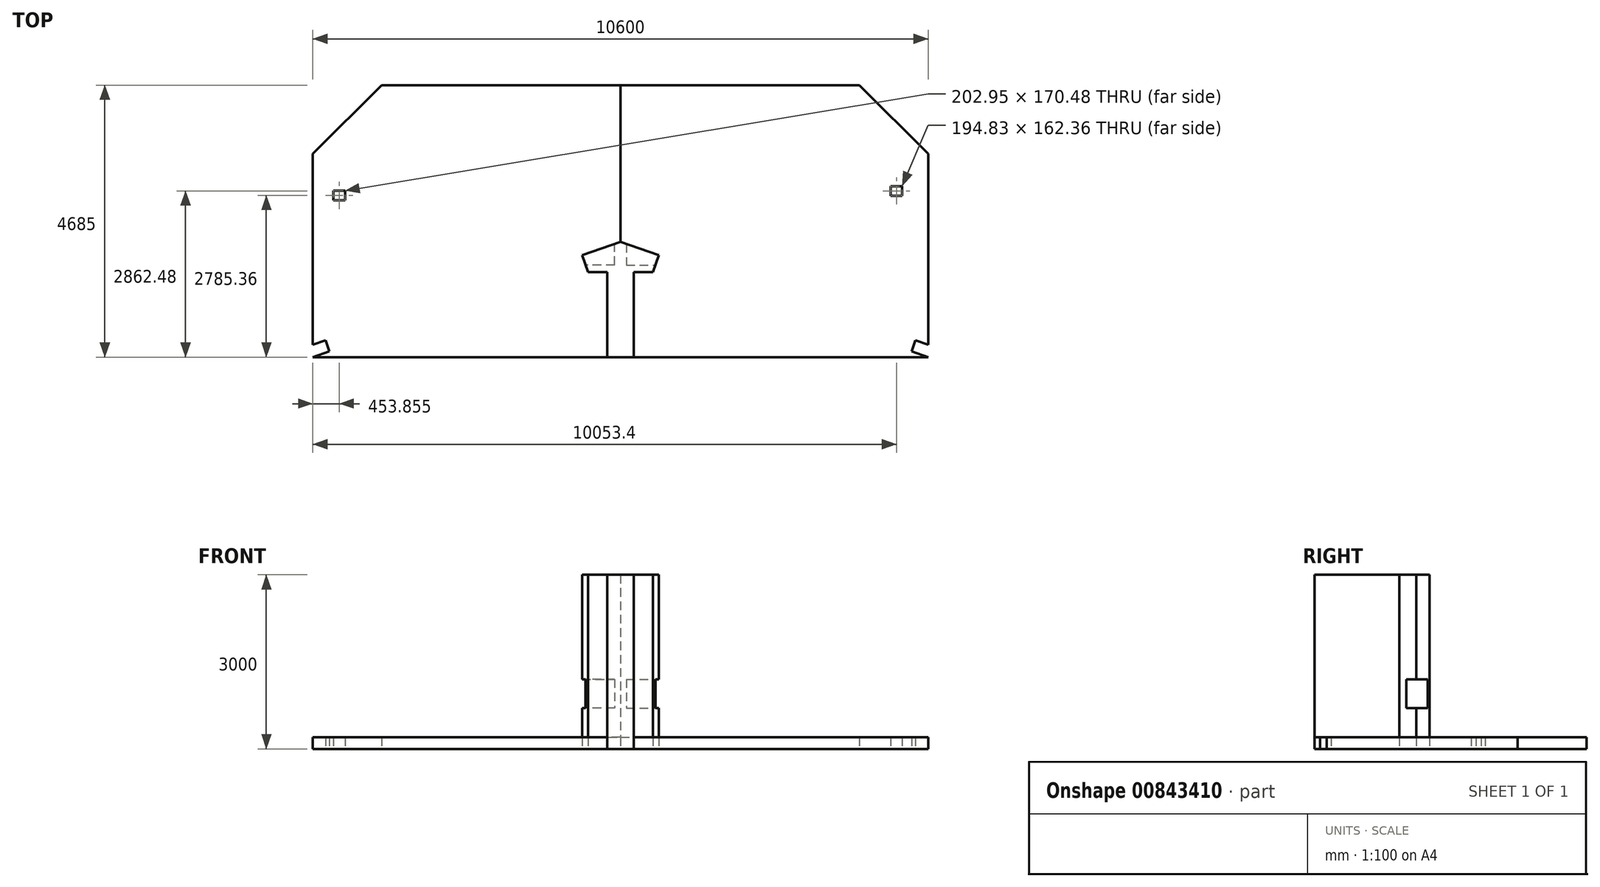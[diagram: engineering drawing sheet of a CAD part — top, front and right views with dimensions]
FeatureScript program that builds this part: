
annotation { "Feature Type Name" : "Feature", "Feature Type Description" : "" }
export const myFeature = defineFeature(function(context is Context, id is Id, definition is map)
    precondition{}
    {
        {
            var Q0;
            Q0=qCreatedBy(makeId("Top.planeOp"),FACE);
            var sketch = newSketch(context, id + "F0", { "sketchPlane" : qUnion([Q0])});
            skLineSegment(sketch, "E0.bottom", {"start": v(-2879.78, 2584.02) * mm, "end": v(-1580.4, 2584.02) * mm});
            skLineSegment(sketch, "E0.top", {"start": v(-2879.78, 1773.08) * mm, "end": v(-1580.4, 1773.08) * mm});
            skLineSegment(sketch, "E0.left", {"start": v(-2879.78, 2584.02) * mm, "end": v(-2879.78, 1773.08) * mm});
            skLineSegment(sketch, "E0.right", {"start": v(-1580.4, 2584.02) * mm, "end": v(-1580.4, 1773.08) * mm});
            skLineSegment(sketch, "E1.bottom", {"start": v(291.18, 2556.08) * mm, "end": v(2223.4, 2556.08) * mm});
            skLineSegment(sketch, "E1.top", {"start": v(291.18, 1660.2) * mm, "end": v(2223.4, 1660.2) * mm});
            skLineSegment(sketch, "E1.left", {"start": v(291.18, 2556.08) * mm, "end": v(291.18, 1660.2) * mm});
            skLineSegment(sketch, "E1.right", {"start": v(2223.4, 2556.08) * mm, "end": v(2223.4, 1660.2) * mm});
            skLineSegment(sketch, "E2.bottom", {"start": v(3957.7, 594.24) * mm, "end": v(4737.35, 594.24) * mm});
            skLineSegment(sketch, "E2.top", {"start": v(3957.7, -525.95) * mm, "end": v(4737.35, -525.95) * mm});
            skLineSegment(sketch, "E2.left", {"start": v(3957.7, 594.24) * mm, "end": v(3957.7, -525.95) * mm});
            skLineSegment(sketch, "E2.right", {"start": v(4737.35, 594.24) * mm, "end": v(4737.35, -525.95) * mm});
            skLineSegment(sketch, "E3.bottom", {"start": v(-4506.24, -591.91) * mm, "end": v(-3473.46, -591.91) * mm});
            skLineSegment(sketch, "E3.top", {"start": v(-4506.24, -1546.94) * mm, "end": v(-3473.46, -1546.94) * mm});
            skLineSegment(sketch, "E3.left", {"start": v(-4506.24, -591.91) * mm, "end": v(-4506.24, -1546.94) * mm});
            skLineSegment(sketch, "E3.right", {"start": v(-3473.46, -591.91) * mm, "end": v(-3473.46, -1546.94) * mm});
            skSolve(sketch);
        }
        {
            var Q0;
            Q0=qCreatedBy(makeId("Top.planeOp"),FACE);
            var sketch = newSketch(context, id + "F1", { "sketchPlane" : qUnion([Q0])});
            skLineSegment(sketch, "E4.bottom", {"start": v(-4115, 2342.5) * mm, "end": v(4115, 2342.5) * mm});
            skLineSegment(sketch, "E4.top", {"start": v(-5300, -2342.5) * mm, "end": v(-230.94, -2342.5) * mm});
            skLineSegment(sketch, "E4.left", {"start": v(-5300, 1157.5) * mm, "end": v(-5300, -2342.5) * mm});
            skLineSegment(sketch, "E4.right", {"start": v(5300, 1157.5) * mm, "end": v(5300, -2342.5) * mm});
            skPoint(sketch, "E4.middle", {"position": v(0, 0) * mm});
            skLineSegment(sketch, "E5", {"start": v(-5300, 1157.5) * mm, "end": v(-4115, 2342.5) * mm});
            skLineSegment(sketch, "E6", {"start": v(4115, 2342.5) * mm, "end": v(5300, 1157.5) * mm});
            skPoint(sketch, "E7.orphan", {"position": v(5300, 2342.5) * mm});
            skPoint(sketch, "E8.orphan", {"position": v(-5300, 2342.5) * mm});
            skLineSegment(sketch, "E9", {"start": v(0, -357.5) * mm, "end": v(661.86, -585.4) * mm});
            skLineSegment(sketch, "E10", {"start": v(0, -357.5) * mm, "end": v(-661.86, -585.4) * mm});
            skLineSegment(sketch, "E11", {"start": v(-661.86, -585.4) * mm, "end": v(-560.94, -878.5) * mm});
            skLineSegment(sketch, "E12", {"start": v(-230.94, -878.5) * mm, "end": v(-230.94, -2342.5) * mm});
            skLineSegment(sketch, "E13", {"start": v(0, 0) * mm, "end": v(0, 2342.5) * mm, "construction": true});
            skLineSegment(sketch, "E14.MirrorCS", {"start": v(230.94, -878.5) * mm, "end": v(230.94, -2342.5) * mm});
            skLineSegment(sketch, "E15.MirrorCS", {"start": v(661.86, -585.4) * mm, "end": v(560.94, -878.5) * mm});
            skLineSegment(sketch, "E16.MirrorCS", {"start": v(560.94, -878.5) * mm, "end": v(230.94, -878.5) * mm});
            skLineSegment(sketch, "E17.trimOffspring", {"start": v(230.94, -2342.5) * mm, "end": v(5300, -2342.5) * mm});
            skLineSegment(sketch, "E18", {"start": v(-230.94, -878.5) * mm, "end": v(-560.94, -878.5) * mm});
            skLineSegment(sketch, "E19.bottom", {"start": v(4850.85, 601.16) * mm, "end": v(4656.02, 601.16) * mm});
            skLineSegment(sketch, "E19.top", {"start": v(4850.85, 438.8) * mm, "end": v(4656.02, 438.8) * mm});
            skLineSegment(sketch, "E19.left", {"start": v(4850.85, 601.16) * mm, "end": v(4850.85, 438.8) * mm});
            skLineSegment(sketch, "E19.right", {"start": v(4656.02, 601.16) * mm, "end": v(4656.02, 438.8) * mm});
            skLineSegment(sketch, "E20.bottom", {"start": v(-4947.62, 528.1) * mm, "end": v(-4744.67, 528.1) * mm});
            skLineSegment(sketch, "E20.top", {"start": v(-4947.62, 357.62) * mm, "end": v(-4744.67, 357.62) * mm});
            skLineSegment(sketch, "E20.left", {"start": v(-4947.62, 528.1) * mm, "end": v(-4947.62, 357.62) * mm});
            skLineSegment(sketch, "E20.right", {"start": v(-4744.67, 528.1) * mm, "end": v(-4744.67, 357.62) * mm});
            skLineSegment(sketch, "E21", {"start": v(-230.94, -2342.5) * mm, "end": v(230.94, -2342.5) * mm});
            skLineSegment(sketch, "E22", {"start": v(-5300, -2130.98) * mm, "end": v(-5081.46, -2055.73) * mm});
            skLineSegment(sketch, "E23", {"start": v(-5081.46, -2055.73) * mm, "end": v(-5016.34, -2244.83) * mm});
            skLineSegment(sketch, "E24", {"start": v(-5016.34, -2244.83) * mm, "end": v(-5300, -2342.5) * mm});
            skLineSegment(sketch, "E25.MirrorCS", {"start": v(5016.34, -2244.83) * mm, "end": v(5300, -2342.5) * mm});
            skLineSegment(sketch, "E26.MirrorCS", {"start": v(5300, -2130.98) * mm, "end": v(5081.46, -2055.73) * mm});
            skLineSegment(sketch, "E27.MirrorCS", {"start": v(5081.46, -2055.73) * mm, "end": v(5016.34, -2244.83) * mm});
            skLineSegment(sketch, "E28", {"start": v(0, -357.5) * mm, "end": v(0, 2342.5) * mm});
            skSolve(sketch);
        }
        {
            var Q0;
            Q0=makeQuery(id+"F1.imprint","IMPRINT",FACE,{"disambiguationData":[TD([[makeQuery(id+"F1.imprint","IMPRINT",EDGE,{"derivedFrom":sQuery(id+"F1.wireOp",EDGE,"E4.top")}),1.0]])]});
            extrude(context, id + "F2", {"entities" : qUnion([Q0]), "depth" : 200 * mm, "offsetDistance" : 25 * mm});
        }
        {
            var Q0;
            {var subQ0=sQuery(id+"F1.wireOp",EDGE,"E6");Q0=makeQuery(id+"F1.imprint","IMPRINT",FACE,{"disambiguationData":[TD([[makeQuery(id+"F1.imprint","IMPRINT",EDGE,{"derivedFrom":subQ0}),-1.0]])]});}
            extrude(context, id + "F3", {"entities" : qUnion([Q0]), "depth" : 200 * mm, "offsetDistance" : 25 * mm});
        }
        {
            var Q0;
            Q0=makeQuery(id+"F1.imprint","IMPRINT",FACE,{"disambiguationData":[TD([[makeQuery(id+"F1.imprint","IMPRINT",EDGE,{"derivedFrom":sQuery(id+"F1.wireOp",EDGE,"E11")}),1.0]])]});
            extrude(context, id + "F4", {"entities" : qUnion([Q0]), "depth" : 3000 * mm, "offsetDistance" : 25 * mm});
        }
        {
            var Q0;
            Q0=makeQuery(id+"F2.opExtrude","CAP_FACE",FACE,{"disambiguationData":[OSD([sQuery(id+"F1.wireOp",EDGE,"E4.bottom"),sQuery(id+"F1.wireOp",EDGE,"E4.top"),sQuery(id+"F1.wireOp",EDGE,"E4.left"),sQuery(id+"F1.wireOp",EDGE,"E5"),sQuery(id+"F1.wireOp",EDGE,"E11"),sQuery(id+"F1.wireOp",EDGE,"E12"),sQuery(id+"F1.wireOp",EDGE,"E10"),sQuery(id+"F1.wireOp",EDGE,"E18"),sQuery(id+"F1.wireOp",EDGE,"E20.bottom"),sQuery(id+"F1.wireOp",EDGE,"E20.top"),sQuery(id+"F1.wireOp",EDGE,"E20.left"),sQuery(id+"F1.wireOp",EDGE,"E20.right"),sQuery(id+"F1.wireOp",EDGE,"E22"),sQuery(id+"F1.wireOp",EDGE,"E23"),sQuery(id+"F1.wireOp",EDGE,"E24"),sQuery(id+"F1.wireOp",EDGE,"E28")])],"isStart":false});
            var sketch = newSketch(context, id + "F5", { "sketchPlane" : qUnion([Q0])});
            skLineSegment(sketch, "E29.bottom", {"start": v(-700, 2342.5) * mm, "end": v(700, 2342.5) * mm});
            skLineSegment(sketch, "E29.top", {"start": v(-700, 1642.5) * mm, "end": v(700, 1642.5) * mm});
            skLineSegment(sketch, "E29.left", {"start": v(-700, 2342.5) * mm, "end": v(-700, 1642.5) * mm});
            skLineSegment(sketch, "E29.right", {"start": v(700, 2342.5) * mm, "end": v(700, 1642.5) * mm});
            skLineSegment(sketch, "E30", {"start": v(-661.86, -585.4) * mm, "end": v(661.86, -585.4) * mm});
            skLineSegment(sketch, "E31", {"start": v(-700, 1642.5) * mm, "end": v(-700, -757.5) * mm});
            skLineSegment(sketch, "E32", {"start": v(700, 1642.5) * mm, "end": v(700, -757.5) * mm});
            skLineSegment(sketch, "E33", {"start": v(0, -757.5) * mm, "end": v(0, 1642.5) * mm});
            skLineSegment(sketch, "E34", {"start": v(-700, -757.5) * mm, "end": v(700, -757.5) * mm});
            skLineSegment(sketch, "E35", {"start": v(-661.86, -757.5) * mm, "end": v(-661.86, -585.4) * mm});
            skLineSegment(sketch, "E36", {"start": v(-661.86, -757.5) * mm, "end": v(0, -757.5) * mm});
            skLineSegment(sketch, "E37.MirrorCS", {"start": v(661.86, -757.5) * mm, "end": v(0, -757.5) * mm});
            skLineSegment(sketch, "E38.MirrorCS", {"start": v(661.86, -757.5) * mm, "end": v(661.86, -585.4) * mm});
            skLineSegment(sketch, "E39", {"start": v(661.86, -585.4) * mm, "end": v(0, -357.5) * mm});
            skLineSegment(sketch, "E40", {"start": v(0, -357.5) * mm, "end": v(-661.86, -585.4) * mm});
            skSolve(sketch);
        }
        {
            var Q0;
            {var subQ3=sQuery(id+"F5.wireOp",EDGE,"E29.left");Q0=makeQuery(id+"F5.imprint","IMPRINT",FACE,{"disambiguationData":[TD([[makeQuery(id+"F5.imprint","IMPRINT",EDGE,{"derivedFrom":subQ3}),1.0]])]});}
            var Q1;
            {var subQ3=sQuery(id+"F5.wireOp",EDGE,"E29.right");Q1=makeQuery(id+"F5.imprint","IMPRINT",FACE,{"disambiguationData":[TD([[makeQuery(id+"F5.imprint","IMPRINT",EDGE,{"derivedFrom":subQ3}),-1.0]])]});}
            extrude(context, id + "F6", {"entities" : qUnion([Q0, Q1]), "depth" : 500 * mm, "offsetDistance" : 25 * mm});
        }
        {
            var Q0;
            {var subQ1=sQuery(id+"F5.wireOp",EDGE,"E32");Q0=makeQuery(id+"F5.imprint","IMPRINT",FACE,{"disambiguationData":[TD([[makeQuery(id+"F5.imprint","IMPRINT",EDGE,{"derivedFrom":subQ1}),-1.0]])]});}
            extrude(context, id + "F7", {"entities" : qUnion([Q0]), "depth" : 1000 * mm, "offsetDistance" : 25 * mm});
        }
        {
            var Q0;
            {var subQ1=sQuery(id+"F5.wireOp",EDGE,"E31");Q0=makeQuery(id+"F5.imprint","IMPRINT",FACE,{"disambiguationData":[TD([[makeQuery(id+"F5.imprint","IMPRINT",EDGE,{"derivedFrom":subQ1}),1.0]])]});}
            extrude(context, id + "F8", {"entities" : qUnion([Q0]), "depth" : 1000 * mm, "offsetDistance" : 25 * mm});
        }
        {
            var Q0;
            {var subQ0=sQuery(id+"F5.wireOp",EDGE,"E37.MirrorCS");Q0=makeQuery(id+"F5.imprint","IMPRINT",FACE,{"disambiguationData":[TD([[makeQuery(id+"F5.imprint","IMPRINT",EDGE,{"derivedFrom":subQ0}),1.0]])]});}
            var Q1;
            Q1=makeQuery(id+"F5.imprint","IMPRINT",FACE,{"disambiguationData":[TD([[makeQuery(id+"F5.imprint","IMPRINT",EDGE,{"derivedFrom":sQuery(id+"F5.wireOp",EDGE,"E35")}),-1.0]])]});
            extrude(context, id + "F9", {"entities" : qUnion([Q0, Q1]), "depth" : 1000 * mm, "offsetDistance" : 25 * mm});
        }
        {
            var Q0;
            Q0=makeQuery(id+"F7.opExtrude","SWEPT_FACE",FACE,{"disambiguationData":[OSD([sQuery(id+"F5.wireOp",EDGE,"E32")])]});
            var sketch = newSketch(context, id + "F10", { "sketchPlane" : qUnion([Q0])});
            skLineSegment(sketch, "E41.bottom", {"start": v(1642.5, 1200) * mm, "end": v(-757.5, 1200) * mm});
            skLineSegment(sketch, "E41.top", {"start": v(1642.5, 700) * mm, "end": v(-757.5, 700) * mm});
            skLineSegment(sketch, "E41.left", {"start": v(1642.5, 1200) * mm, "end": v(1642.5, 700) * mm});
            skLineSegment(sketch, "E41.right", {"start": v(-757.5, 1200) * mm, "end": v(-757.5, 700) * mm});
            skSolve(sketch);
        }
        {
            var Q0;
            Q0 = qSketchRegion(id + "F10", true);
            extrude(context, id + "F11", {"entities" : qUnion([Q0]), "operationType" : NewBodyOperationType.REMOVE, "oppositeDirection" : true, "depth" : 600 * mm, "offsetDistance" : 25 * mm});
        }
        {
            var Q0;
            Q0=makeQuery(id+"F8.opExtrude","SWEPT_FACE",FACE,{"disambiguationData":[OSD([sQuery(id+"F5.wireOp",EDGE,"E31")])]});
            var sketch = newSketch(context, id + "F12", { "sketchPlane" : qUnion([Q0])});
            skLineSegment(sketch, "E42.bottom", {"start": v(757.5, 1200) * mm, "end": v(-1642.5, 1200) * mm});
            skLineSegment(sketch, "E42.top", {"start": v(757.5, 700) * mm, "end": v(-1642.5, 700) * mm});
            skLineSegment(sketch, "E42.left", {"start": v(757.5, 1200) * mm, "end": v(757.5, 700) * mm});
            skLineSegment(sketch, "E42.right", {"start": v(-1642.5, 1200) * mm, "end": v(-1642.5, 700) * mm});
            skSolve(sketch);
        }
        {
            var Q0;
            Q0 = qSketchRegion(id + "F12", true);
            extrude(context, id + "F13", {"entities" : qUnion([Q0]), "operationType" : NewBodyOperationType.REMOVE, "oppositeDirection" : true, "depth" : 600 * mm, "offsetDistance" : 25 * mm});
        }
        {
            var Q0;
            Q0=makeQuery(id+"F6.opExtrude","CAP_FACE",FACE,{"disambiguationData":[OSD([sQuery(id+"F5.wireOp",EDGE,"E29.bottom"),sQuery(id+"F5.wireOp",EDGE,"E29.top"),sQuery(id+"F5.wireOp",EDGE,"E29.left"),sQuery(id+"F5.wireOp",EDGE,"E29.right")])],"isStart":false});
            var sketch = newSketch(context, id + "F14", { "sketchPlane" : qUnion([Q0])});
            skLineSegment(sketch, "E43.bottom", {"start": v(100, 1642.5) * mm, "end": v(-100, 1642.5) * mm});
            skLineSegment(sketch, "E43.top", {"start": v(100, 2342.5) * mm, "end": v(-100, 2342.5) * mm});
            skLineSegment(sketch, "E43.left", {"start": v(100, 1642.5) * mm, "end": v(100, 2342.5) * mm});
            skLineSegment(sketch, "E43.right", {"start": v(-100, 1642.5) * mm, "end": v(-100, 2342.5) * mm});
            skSolve(sketch);
        }
        {
            var Q0;
            Q0 = qSketchRegion(id + "F14", true);
            var Q1;
            Q1=makeQuery(id+"F8.opExtrude","CAP_FACE",FACE,{"disambiguationData":[OSD([sQuery(id+"F5.wireOp",EDGE,"E29.top"),sQuery(id+"F5.wireOp",EDGE,"E31"),sQuery(id+"F5.wireOp",EDGE,"E33"),sQuery(id+"F5.wireOp",EDGE,"E34"),sQuery(id+"F5.wireOp",EDGE,"E36")])],"isStart":false});
            extrude(context, id + "F15", {"entities" : qUnion([Q0]), "endBound" : BoundingType.UP_TO_SURFACE, "depth" : 25 * mm, "endBoundEntityFace" : qUnion([Q1]), "offsetDistance" : 25 * mm});
        }
        {
            var Q0;
            Q0=makeQuery(id+"F7.opExtrude","SWEPT_BODY",BODY,{"disambiguationData":[OSD([sQuery(id+"F5.wireOp",EDGE,"E29.top"),sQuery(id+"F5.wireOp",EDGE,"E32"),sQuery(id+"F5.wireOp",EDGE,"E33"),sQuery(id+"F5.wireOp",EDGE,"E34"),sQuery(id+"F5.wireOp",EDGE,"E37.MirrorCS")])]});
            deleteBodies(context, id + "F16", {"entities" : qUnion([Q0])});
        }
        {
            var Q0;
            Q0=makeQuery(id+"F8.opExtrude","SWEPT_BODY",BODY,{"disambiguationData":[OSD([sQuery(id+"F5.wireOp",EDGE,"E29.top"),sQuery(id+"F5.wireOp",EDGE,"E31"),sQuery(id+"F5.wireOp",EDGE,"E33"),sQuery(id+"F5.wireOp",EDGE,"E34"),sQuery(id+"F5.wireOp",EDGE,"E36")])]});
            deleteBodies(context, id + "F17", {"entities" : qUnion([Q0])});
        }
        {
            var Q0;
            Q0=makeQuery(id+"F9.opExtrude","SWEPT_BODY",BODY,{"disambiguationData":[OSD([sQuery(id+"F5.wireOp",EDGE,"E35"),sQuery(id+"F5.wireOp",EDGE,"E36"),sQuery(id+"F5.wireOp",EDGE,"E37.MirrorCS"),sQuery(id+"F5.wireOp",EDGE,"E38.MirrorCS"),sQuery(id+"F5.wireOp",EDGE,"E39"),sQuery(id+"F5.wireOp",EDGE,"E40")])]});
            deleteBodies(context, id + "F18", {"entities" : qUnion([Q0])});
        }
        {
            var Q0;
            Q0=makeQuery(id+"F6.opExtrude","SWEPT_BODY",BODY,{"disambiguationData":[OSD([sQuery(id+"F5.wireOp",EDGE,"E29.bottom"),sQuery(id+"F5.wireOp",EDGE,"E29.top"),sQuery(id+"F5.wireOp",EDGE,"E29.left"),sQuery(id+"F5.wireOp",EDGE,"E29.right")])]});
            deleteBodies(context, id + "F19", {"entities" : qUnion([Q0])});
        }
        {
            var Q0;
            Q0=makeQuery(id+"F15.opExtrude","SWEPT_BODY",BODY,{"disambiguationData":[OSD([sQuery(id+"F14.wireOp",EDGE,"E43.bottom"),sQuery(id+"F14.wireOp",EDGE,"E43.top"),sQuery(id+"F14.wireOp",EDGE,"E43.left"),sQuery(id+"F14.wireOp",EDGE,"E43.right")])]});
            deleteBodies(context, id + "F20", {"entities" : qUnion([Q0])});
        }
    });
